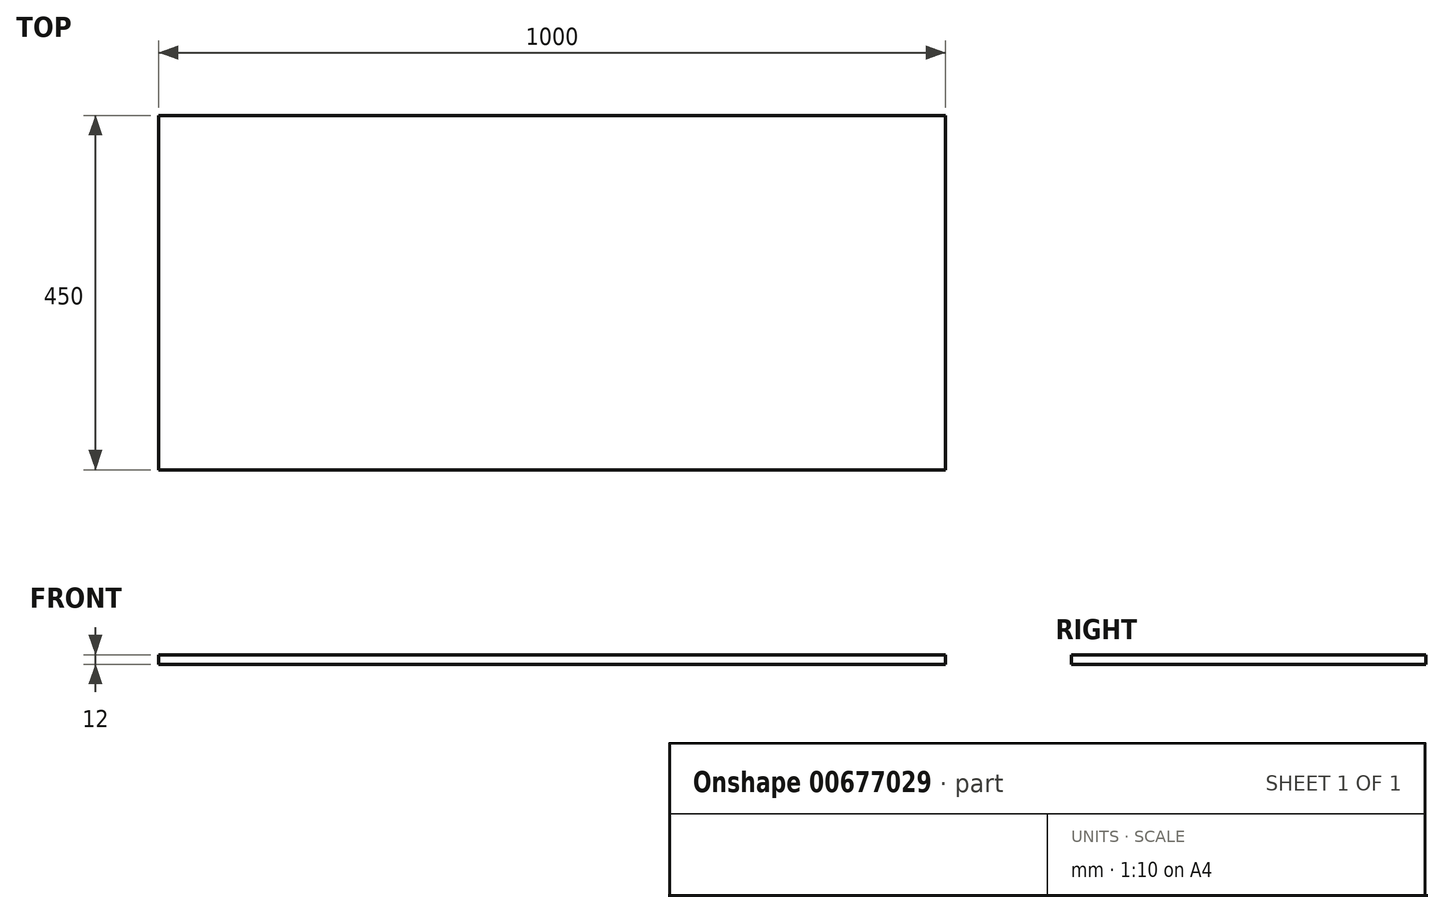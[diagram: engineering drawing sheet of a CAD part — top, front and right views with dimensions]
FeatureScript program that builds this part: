
annotation { "Feature Type Name" : "Feature", "Feature Type Description" : "" }
export const myFeature = defineFeature(function(context is Context, id is Id, definition is map)
    precondition{}
    {
        {
            var Q0;
            Q0=qCreatedBy(makeId("Top.planeOp"),FACE);
            var sketch = newSketch(context, id + "F0", { "sketchPlane" : qUnion([Q0])});
            skLineSegment(sketch, "E0.bottom", {"start": v(0, 0) * mm, "end": v(1000, 0) * mm});
            skLineSegment(sketch, "E0.top", {"start": v(0, -450) * mm, "end": v(1000, -450) * mm});
            skLineSegment(sketch, "E0.left", {"start": v(0, 0) * mm, "end": v(0, -450) * mm});
            skLineSegment(sketch, "E0.right", {"start": v(1000, 0) * mm, "end": v(1000, -450) * mm});
            skSolve(sketch);
        }
        {
            var Q0;
            Q0 = qSketchRegion(id + "F0", true);
            extrude(context, id + "F1", {"entities" : qUnion([Q0]), "depth" : 12 * mm, "offsetDistance" : 25 * mm});
        }
    });
